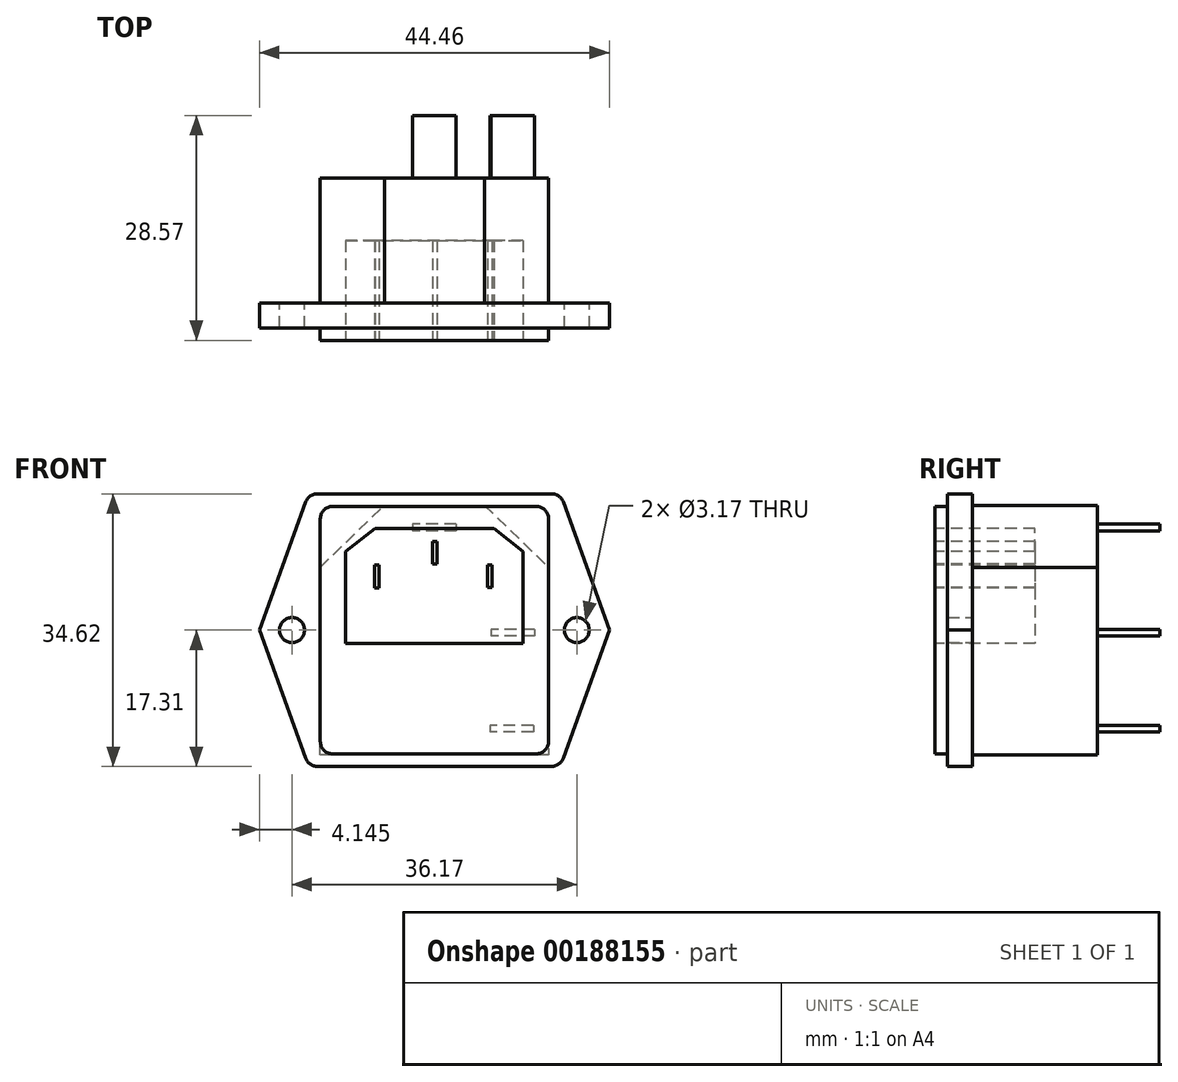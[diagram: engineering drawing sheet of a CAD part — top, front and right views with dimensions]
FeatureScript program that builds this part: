
annotation { "Feature Type Name" : "Feature", "Feature Type Description" : "" }
export const myFeature = defineFeature(function(context is Context, id is Id, definition is map)
    precondition{}
    {
        {
            var Q0;
            Q0=qCreatedBy(makeId("Front.planeOp"),FACE);
            var sketch = newSketch(context, id + "F0", { "sketchPlane" : qUnion([Q0])});
            skLineSegment(sketch, "E0.2", {"start": v(14.88, 17.3) * mm, "end": v(-14.88, 17.3) * mm});
            skLineSegment(sketch, "E0.7", {"start": v(-14.88, -17.3) * mm, "end": v(14.88, -17.3) * mm});
            skLineSegment(sketch, "E1", {"start": v(-16.37, 16.26) * mm, "end": v(-22.23, 0) * mm});
            skLineSegment(sketch, "E2", {"start": v(-22.22, 0) * mm, "end": v(-16.37, -16.26) * mm});
            skLineSegment(sketch, "E3", {"start": v(16.37, 16.26) * mm, "end": v(22.23, 0) * mm});
            skLineSegment(sketch, "E4", {"start": v(22.22, 0) * mm, "end": v(16.37, -16.26) * mm});
            skPoint(sketch, "E5", {"position": v(-16.09, 0) * mm});
            skPoint(sketch, "E6", {"position": v(14.5, 0) * mm});
            skPoint(sketch, "E7", {"position": v(16.09, 0) * mm});
            skPoint(sketch, "E8.visualSharp", {"position": v(-16, 17.3) * mm});
            skArc(sketch, "E8.filletArc", {"start": v(-14.88, 17.3) * mm, "mid": v(-15.8, 17.02) * mm, "end": v(-16.37, 16.26) * mm});
            skPoint(sketch, "E9.visualSharp", {"position": v(-16, -17.3) * mm});
            skArc(sketch, "E9.filletArc", {"start": v(-16.37, -16.26) * mm, "mid": v(-15.8, -17.02) * mm, "end": v(-14.88, -17.3) * mm});
            skPoint(sketch, "E10.visualSharp", {"position": v(16, -17.3) * mm});
            skArc(sketch, "E10.filletArc", {"start": v(14.88, -17.3) * mm, "mid": v(15.8, -17.02) * mm, "end": v(16.37, -16.26) * mm});
            skPoint(sketch, "E11.visualSharp", {"position": v(16, 17.3) * mm});
            skArc(sketch, "E11.filletArc", {"start": v(16.37, 16.26) * mm, "mid": v(15.8, 17.02) * mm, "end": v(14.88, 17.3) * mm});
            skPoint(sketch, "E12", {"position": v(0, 0) * mm});
            skCircle(sketch, "E13", {"center": v(-18.08, 0) * mm, "radius": 1.59 * mm});
            skCircle(sketch, "E14", {"center": v(18.08, 0) * mm, "radius": 1.59 * mm});
            skLineSegment(sketch, "E15.bottom", {"start": v(-12.91, 15.72) * mm, "end": v(12.91, 15.72) * mm});
            skLineSegment(sketch, "E15.top", {"start": v(-12.91, -15.72) * mm, "end": v(12.91, -15.72) * mm});
            skLineSegment(sketch, "E15.left", {"start": v(-14.5, 14.13) * mm, "end": v(-14.5, -14.13) * mm});
            skLineSegment(sketch, "E15.right", {"start": v(14.5, 14.13) * mm, "end": v(14.5, -14.13) * mm});
            skPoint(sketch, "E16", {"position": v(-14.5, 0) * mm});
            skPoint(sketch, "E17.visualSharp", {"position": v(-14.5, 15.72) * mm});
            skArc(sketch, "E17.filletArc", {"start": v(-12.91, 15.72) * mm, "mid": v(-14.04, 15.26) * mm, "end": v(-14.5, 14.13) * mm});
            skPoint(sketch, "E18.visualSharp", {"position": v(14.5, 15.72) * mm});
            skArc(sketch, "E18.filletArc", {"start": v(14.5, 14.13) * mm, "mid": v(14.04, 15.26) * mm, "end": v(12.91, 15.72) * mm});
            skPoint(sketch, "E19.visualSharp", {"position": v(14.5, -15.72) * mm});
            skArc(sketch, "E19.filletArc", {"start": v(12.91, -15.72) * mm, "mid": v(14.04, -15.26) * mm, "end": v(14.5, -14.13) * mm});
            skPoint(sketch, "E20.visualSharp", {"position": v(-14.5, -15.72) * mm});
            skArc(sketch, "E20.filletArc", {"start": v(-14.5, -14.13) * mm, "mid": v(-14.04, -15.26) * mm, "end": v(-12.91, -15.72) * mm});
            skLineSegment(sketch, "E21", {"start": v(0, 17.3) * mm, "end": v(0, -17.3) * mm, "construction": true});
            skLineSegment(sketch, "E22", {"start": v(-18.08, 0) * mm, "end": v(0, 0) * mm, "construction": true});
            skLineSegment(sketch, "E23", {"start": v(0, 0) * mm, "end": v(18.08, 0) * mm, "construction": true});
            skLineSegment(sketch, "E24", {"start": v(-22.23, 0) * mm, "end": v(-18.08, 0) * mm, "construction": true});
            skLineSegment(sketch, "E25", {"start": v(18.08, 0) * mm, "end": v(22.22, 0) * mm, "construction": true});
            skSolve(sketch);
        }
        {
            var Q0;
            Q0=makeQuery(id+"F0.imprint","IMPRINT",FACE,{"disambiguationData":[TD([[makeQuery(id+"F0.imprint","IMPRINT",EDGE,{"derivedFrom":sQuery(id+"F0.wireOp",EDGE,"E0.2")}),1.0]])]});
            var Q1;
            Q1=makeQuery(id+"F0.imprint","IMPRINT",FACE,{"disambiguationData":[TD([[makeQuery(id+"F0.imprint","IMPRINT",EDGE,{"derivedFrom":sQuery(id+"F0.wireOp",EDGE,"E15.bottom")}),-1.0]])]});
            var Q2;
            Q2=sQuery(id+"F0.wireOp",EDGE,"E3");
            var Q3;
            Q3=sQuery(id+"F0.wireOp",EDGE,"E11.filletArc");
            var Q4;
            Q4=sQuery(id+"F0.wireOp",EDGE,"E0.2");
            var Q5;
            Q5=sQuery(id+"F0.wireOp",EDGE,"E8.filletArc");
            var Q6;
            Q6=sQuery(id+"F0.wireOp",EDGE,"E1");
            var Q7;
            Q7=sQuery(id+"F0.wireOp",EDGE,"E2");
            var Q8;
            Q8=sQuery(id+"F0.wireOp",EDGE,"E9.filletArc");
            var Q9;
            Q9=sQuery(id+"F0.wireOp",EDGE,"E0.7");
            var Q10;
            Q10=sQuery(id+"F0.wireOp",EDGE,"E10.filletArc");
            var Q11;
            Q11=sQuery(id+"F0.wireOp",EDGE,"E4");
            var Q12;
            Q12=sQuery(id+"F0.wireOp",EDGE,"E14");
            var Q13;
            Q13=sQuery(id+"F0.wireOp",EDGE,"E13");
            extrude(context, id + "F1", {"entities" : qUnion([Q0, Q1]), "surfaceEntities" : qUnion([Q2, Q3, Q4, Q5, Q6, Q7, Q8, Q9, Q10, Q11, Q12, Q13]), "depth" : 3.17 * mm});
        }
        {
            var Q0;
            Q0=makeQuery(id+"F1.opExtrude","CAP_FACE",FACE,{"disambiguationData":[OSD([sQuery(id+"F0.wireOp",EDGE,"E0.2"),sQuery(id+"F0.wireOp",EDGE,"E0.7"),sQuery(id+"F0.wireOp",EDGE,"E1"),sQuery(id+"F0.wireOp",EDGE,"E2"),sQuery(id+"F0.wireOp",EDGE,"E3"),sQuery(id+"F0.wireOp",EDGE,"E4"),sQuery(id+"F0.wireOp",EDGE,"E8.filletArc"),sQuery(id+"F0.wireOp",EDGE,"E9.filletArc"),sQuery(id+"F0.wireOp",EDGE,"E10.filletArc"),sQuery(id+"F0.wireOp",EDGE,"E11.filletArc"),sQuery(id+"F0.wireOp",EDGE,"E13"),sQuery(id+"F0.wireOp",EDGE,"E14")])],"isStart":false});
            var sketch = newSketch(context, id + "F2", { "sketchPlane" : qUnion([Q0])});
            skLineSegment(sketch, "E26.bottom", {"start": v(-12.91, 15.72) * mm, "end": v(12.91, 15.72) * mm});
            skLineSegment(sketch, "E26.top", {"start": v(-12.91, -15.72) * mm, "end": v(12.91, -15.72) * mm});
            skLineSegment(sketch, "E26.left", {"start": v(-14.5, 14.13) * mm, "end": v(-14.5, -14.13) * mm});
            skLineSegment(sketch, "E26.right", {"start": v(14.5, 14.13) * mm, "end": v(14.5, -14.13) * mm});
            skLineSegment(sketch, "E27", {"start": v(-14.5, 0) * mm, "end": v(14.5, 0) * mm, "construction": true});
            skPoint(sketch, "E28", {"position": v(-14.5, 0) * mm});
            skPoint(sketch, "E29.visualSharp", {"position": v(-14.5, 15.72) * mm});
            skArc(sketch, "E29.filletArc", {"start": v(-12.91, 15.72) * mm, "mid": v(-14.04, 15.26) * mm, "end": v(-14.5, 14.13) * mm});
            skPoint(sketch, "E30.visualSharp", {"position": v(14.5, 15.72) * mm});
            skArc(sketch, "E30.filletArc", {"start": v(14.5, 14.13) * mm, "mid": v(14.04, 15.26) * mm, "end": v(12.91, 15.72) * mm});
            skPoint(sketch, "E31.visualSharp", {"position": v(14.5, -15.72) * mm});
            skArc(sketch, "E31.filletArc", {"start": v(12.91, -15.72) * mm, "mid": v(14.04, -15.26) * mm, "end": v(14.5, -14.13) * mm});
            skPoint(sketch, "E32.visualSharp", {"position": v(-14.5, -15.72) * mm});
            skArc(sketch, "E32.filletArc", {"start": v(-14.5, -14.13) * mm, "mid": v(-14.04, -15.26) * mm, "end": v(-12.91, -15.72) * mm});
            skLineSegment(sketch, "E33", {"start": v(0, 15.72) * mm, "end": v(0, -15.72) * mm, "construction": true});
            skPoint(sketch, "E34", {"position": v(0, 0) * mm});
            skSolve(sketch);
        }
        {
            var Q0;
            Q0=makeQuery(id+"F2.imprint","IMPRINT",FACE,{"disambiguationData":[TD([[makeQuery(id+"F2.imprint","IMPRINT",EDGE,{"derivedFrom":sQuery(id+"F2.wireOp",EDGE,"E26.bottom")}),-1.0]])]});
            extrude(context, id + "F3", {"entities" : qUnion([Q0]), "operationType" : NewBodyOperationType.ADD, "depth" : 1.59 * mm});
        }
        {
            var Q0;
            Q0=makeQuery(id+"F1.opExtrude","CAP_FACE",FACE,{"disambiguationData":[OSD([sQuery(id+"F0.wireOp",EDGE,"E0.2"),sQuery(id+"F0.wireOp",EDGE,"E0.7"),sQuery(id+"F0.wireOp",EDGE,"E1"),sQuery(id+"F0.wireOp",EDGE,"E2"),sQuery(id+"F0.wireOp",EDGE,"E3"),sQuery(id+"F0.wireOp",EDGE,"E4"),sQuery(id+"F0.wireOp",EDGE,"E8.filletArc"),sQuery(id+"F0.wireOp",EDGE,"E9.filletArc"),sQuery(id+"F0.wireOp",EDGE,"E10.filletArc"),sQuery(id+"F0.wireOp",EDGE,"E11.filletArc"),sQuery(id+"F0.wireOp",EDGE,"E13"),sQuery(id+"F0.wireOp",EDGE,"E14")])],"isStart":true});
            var sketch = newSketch(context, id + "F4", { "sketchPlane" : qUnion([Q0])});
            skLineSegment(sketch, "E35", {"start": v(-6.35, 15.85) * mm, "end": v(-14.5, 7.96) * mm});
            skLineSegment(sketch, "E36", {"start": v(-14.5, 7.96) * mm, "end": v(-14.5, -15.85) * mm});
            skLineSegment(sketch, "E37", {"start": v(-14.5, -15.85) * mm, "end": v(14.5, -15.85) * mm});
            skLineSegment(sketch, "E38", {"start": v(14.5, -15.85) * mm, "end": v(14.5, 7.96) * mm});
            skLineSegment(sketch, "E39", {"start": v(14.5, 7.96) * mm, "end": v(6.35, 15.85) * mm});
            skLineSegment(sketch, "E40", {"start": v(6.35, 15.85) * mm, "end": v(-6.35, 15.85) * mm});
            skLineSegment(sketch, "E41", {"start": v(0, 15.85) * mm, "end": v(0, -15.85) * mm, "construction": true});
            skPoint(sketch, "E42", {"position": v(0, 0) * mm});
            skSolve(sketch);
        }
        {
            var Q0;
            Q0=makeQuery(id+"F4.imprint","IMPRINT",FACE,{"disambiguationData":[TD([[makeQuery(id+"F4.imprint","IMPRINT",EDGE,{"derivedFrom":sQuery(id+"F4.wireOp",EDGE,"ttAV1aEG-yLhL-jNVv-QrRk-bn4didBpnlfS")}),1.0]])]});
            var Q1;
            Q1=makeQuery(id+"F4.imprint","IMPRINT",FACE,{"disambiguationData":[TD([[makeQuery(id+"F4.imprint","IMPRINT",EDGE,{"derivedFrom":sQuery(id+"F4.wireOp",EDGE,"E35")}),1.0]])]});
            extrude(context, id + "F5", {"entities" : qUnion([Q0, Q1]), "operationType" : NewBodyOperationType.ADD, "depth" : 15.88 * mm});
        }
        {
            var Q0;
            Q0=makeQuery(id+"F5.opExtrude","CAP_FACE",FACE,{"disambiguationData":[OSD([sQuery(id+"F4.wireOp",EDGE,"E35"),sQuery(id+"F4.wireOp",EDGE,"E36"),sQuery(id+"F4.wireOp",EDGE,"E37"),sQuery(id+"F4.wireOp",EDGE,"E38"),sQuery(id+"F4.wireOp",EDGE,"E39"),sQuery(id+"F4.wireOp",EDGE,"E40")])],"isStart":false});
            var sketch = newSketch(context, id + "F6", { "sketchPlane" : qUnion([Q0])});
            skLineSegment(sketch, "E43.bottom", {"start": v(-2.76, 13.46) * mm, "end": v(2.76, 13.46) * mm});
            skLineSegment(sketch, "E43.top", {"start": v(-2.76, 12.62) * mm, "end": v(2.76, 12.62) * mm});
            skLineSegment(sketch, "E43.left", {"start": v(-2.76, 13.46) * mm, "end": v(-2.76, 12.62) * mm});
            skLineSegment(sketch, "E43.right", {"start": v(2.76, 13.46) * mm, "end": v(2.76, 12.62) * mm});
            skLineSegment(sketch, "E44.bottom", {"start": v(-12.56, -12.08) * mm, "end": v(-7.05, -12.08) * mm});
            skLineSegment(sketch, "E44.top", {"start": v(-12.56, -12.93) * mm, "end": v(-7.05, -12.93) * mm});
            skLineSegment(sketch, "E44.left", {"start": v(-12.56, -12.08) * mm, "end": v(-12.56, -12.93) * mm});
            skLineSegment(sketch, "E44.right", {"start": v(-7.05, -12.08) * mm, "end": v(-7.05, -12.93) * mm});
            skLineSegment(sketch, "E45.bottom", {"start": v(-12.72, 0.1) * mm, "end": v(-7.2, 0.1) * mm});
            skLineSegment(sketch, "E45.top", {"start": v(-12.72, -0.75) * mm, "end": v(-7.2, -0.75) * mm});
            skLineSegment(sketch, "E45.left", {"start": v(-12.72, 0.1) * mm, "end": v(-12.72, -0.75) * mm});
            skLineSegment(sketch, "E45.right", {"start": v(-7.2, 0.1) * mm, "end": v(-7.2, -0.75) * mm});
            skSolve(sketch);
        }
        {
            var Q0;
            Q0=makeQuery(id+"F6.imprint","IMPRINT",FACE,{"disambiguationData":[TD([[makeQuery(id+"F6.imprint","IMPRINT",EDGE,{"derivedFrom":sQuery(id+"F6.wireOp",EDGE,"E43.bottom")}),-1.0]])]});
            var Q1;
            Q1=makeQuery(id+"F6.imprint","IMPRINT",FACE,{"disambiguationData":[TD([[makeQuery(id+"F6.imprint","IMPRINT",EDGE,{"derivedFrom":sQuery(id+"F6.wireOp",EDGE,"E45.bottom")}),-1.0]])]});
            var Q2;
            Q2=makeQuery(id+"F6.imprint","IMPRINT",FACE,{"disambiguationData":[TD([[makeQuery(id+"F6.imprint","IMPRINT",EDGE,{"derivedFrom":sQuery(id+"F6.wireOp",EDGE,"E44.bottom")}),-1.0]])]});
            extrude(context, id + "F7", {"entities" : qUnion([Q0, Q1, Q2]), "operationType" : NewBodyOperationType.ADD, "depth" : 7.94 * mm});
        }
        {
            var Q0;
            Q0=makeQuery(id+"F3.opExtrude","CAP_FACE",FACE,{"disambiguationData":[OSD([sQuery(id+"F2.wireOp",EDGE,"E26.bottom"),sQuery(id+"F2.wireOp",EDGE,"E26.top"),sQuery(id+"F2.wireOp",EDGE,"E26.left"),sQuery(id+"F2.wireOp",EDGE,"E26.right"),sQuery(id+"F2.wireOp",EDGE,"E29.filletArc"),sQuery(id+"F2.wireOp",EDGE,"E30.filletArc"),sQuery(id+"F2.wireOp",EDGE,"E31.filletArc"),sQuery(id+"F2.wireOp",EDGE,"E32.filletArc")])],"isStart":false});
            var sketch = newSketch(context, id + "F8", { "sketchPlane" : qUnion([Q0])});
            skLineSegment(sketch, "E46", {"start": v(-11.28, -1.67) * mm, "end": v(11.28, -1.67) * mm});
            skLineSegment(sketch, "E47", {"start": v(11.28, -1.67) * mm, "end": v(11.28, 10) * mm});
            skLineSegment(sketch, "E48", {"start": v(11.28, 10) * mm, "end": v(7.54, 12.89) * mm});
            skLineSegment(sketch, "E49", {"start": v(7.54, 12.89) * mm, "end": v(-7.54, 12.89) * mm});
            skLineSegment(sketch, "E50", {"start": v(-7.54, 12.89) * mm, "end": v(-11.28, 10) * mm});
            skLineSegment(sketch, "E51", {"start": v(-11.28, 10) * mm, "end": v(-11.28, -1.67) * mm});
            skLineSegment(sketch, "E52.bottom", {"start": v(-7.6, 8.26) * mm, "end": v(-7.05, 8.26) * mm});
            skLineSegment(sketch, "E52.top", {"start": v(-7.6, 5.37) * mm, "end": v(-7.05, 5.37) * mm});
            skLineSegment(sketch, "E52.left", {"start": v(-7.6, 8.26) * mm, "end": v(-7.6, 5.37) * mm});
            skLineSegment(sketch, "E52.right", {"start": v(-7.05, 8.26) * mm, "end": v(-7.05, 5.37) * mm});
            skPoint(sketch, "E53", {"position": v(0, 12.89) * mm});
            skPoint(sketch, "E54", {"position": v(0, -1.67) * mm});
            skLineSegment(sketch, "E55.bottom", {"start": v(6.74, 8.28) * mm, "end": v(7.29, 8.28) * mm});
            skLineSegment(sketch, "E55.top", {"start": v(6.74, 5.4) * mm, "end": v(7.29, 5.4) * mm});
            skLineSegment(sketch, "E55.left", {"start": v(6.74, 8.28) * mm, "end": v(6.74, 5.4) * mm});
            skLineSegment(sketch, "E55.right", {"start": v(7.29, 8.28) * mm, "end": v(7.29, 5.4) * mm});
            skLineSegment(sketch, "E56.bottom", {"start": v(-0.23, 11.26) * mm, "end": v(0.32, 11.26) * mm});
            skLineSegment(sketch, "E56.top", {"start": v(-0.23, 8.37) * mm, "end": v(0.32, 8.37) * mm});
            skLineSegment(sketch, "E56.left", {"start": v(-0.23, 11.26) * mm, "end": v(-0.23, 8.37) * mm});
            skLineSegment(sketch, "E56.right", {"start": v(0.32, 11.26) * mm, "end": v(0.32, 8.37) * mm});
            skSolve(sketch);
        }
        {
            var Q0;
            Q0=makeQuery(id+"F8.imprint","IMPRINT",FACE,{"disambiguationData":[TD([[makeQuery(id+"F8.imprint","IMPRINT",EDGE,{"derivedFrom":sQuery(id+"F8.wireOp",EDGE,"E46")}),1.0]])]});
            extrude(context, id + "F9", {"entities" : qUnion([Q0]), "operationType" : NewBodyOperationType.REMOVE, "oppositeDirection" : true, "depth" : 12.7 * mm});
        }
    });
